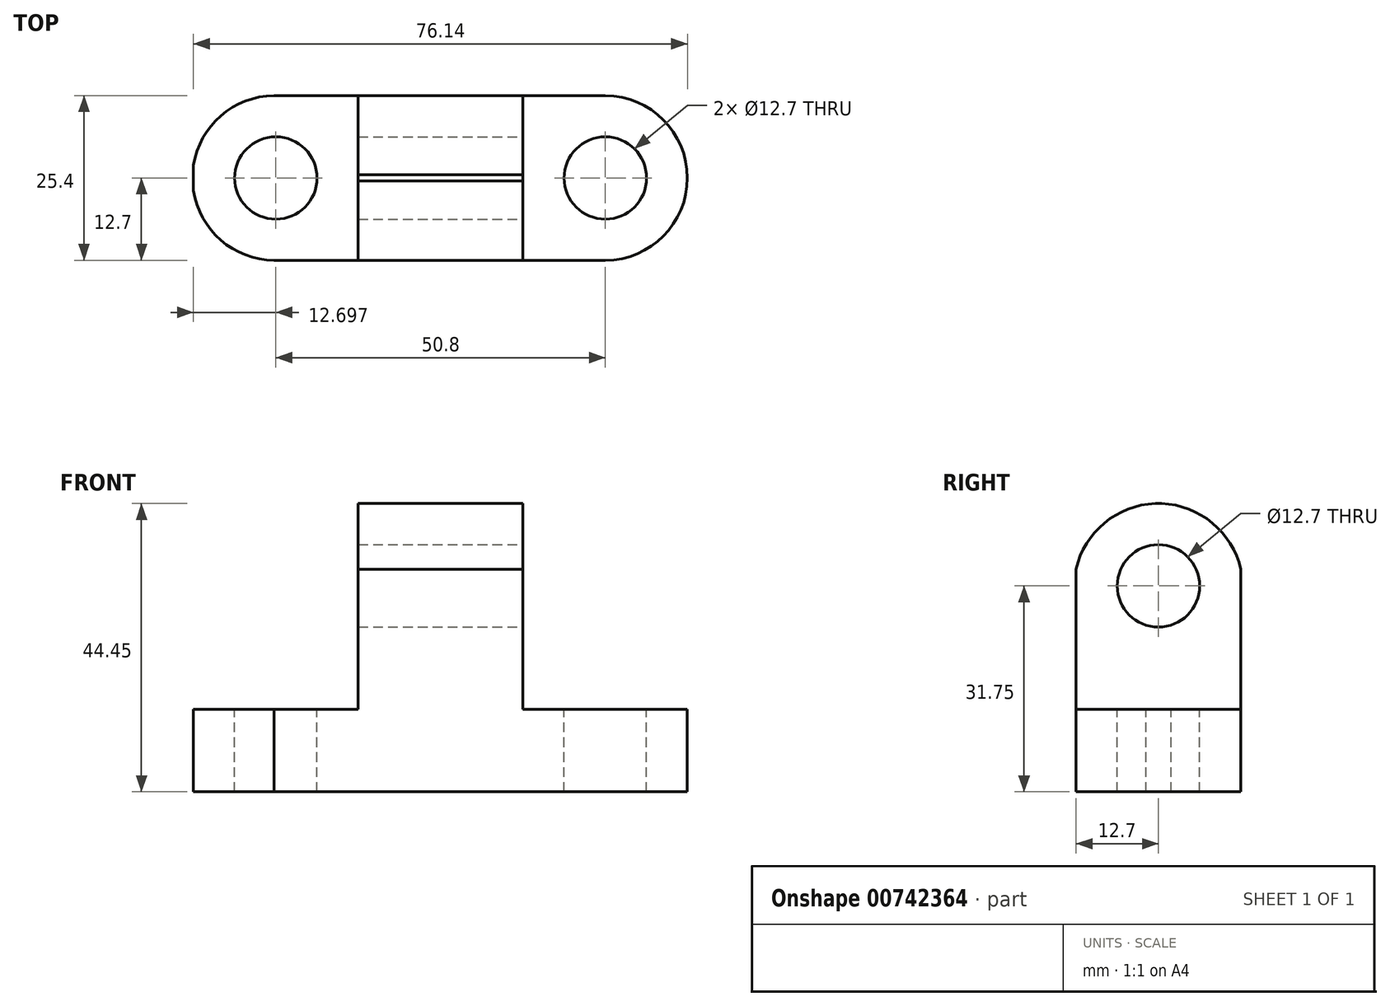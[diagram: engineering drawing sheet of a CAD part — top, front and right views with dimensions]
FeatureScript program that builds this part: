
annotation { "Feature Type Name" : "Feature", "Feature Type Description" : "" }
export const myFeature = defineFeature(function(context is Context, id is Id, definition is map)
    precondition{}
    {
        {
            var Q0;
            Q0=qCreatedBy(makeId("Front.planeOp"),FACE);
            var sketch = newSketch(context, id + "F0", { "sketchPlane" : qUnion([Q0])});
            skLineSegment(sketch, "E0", {"start": v(-40.6, 0) * mm, "end": v(35.6, 0) * mm});
            skLineSegment(sketch, "E1", {"start": v(35.6, 0) * mm, "end": v(35.6, 12.7) * mm});
            skLineSegment(sketch, "E2", {"start": v(35.6, 12.7) * mm, "end": v(10.2, 12.7) * mm});
            skLineSegment(sketch, "E3", {"start": v(10.2, 12.7) * mm, "end": v(10.2, 44.45) * mm});
            skLineSegment(sketch, "E4", {"start": v(10.2, 44.45) * mm, "end": v(-15.2, 44.45) * mm});
            skLineSegment(sketch, "E5", {"start": v(-15.2, 44.45) * mm, "end": v(-15.2, 12.7) * mm});
            skLineSegment(sketch, "E6", {"start": v(-15.2, 12.7) * mm, "end": v(-40.6, 12.7) * mm});
            skLineSegment(sketch, "E7", {"start": v(-40.6, 12.7) * mm, "end": v(-40.6, 0) * mm});
            skSolve(sketch);
        }
        {
            var Q0;
            Q0=makeQuery(id+"F0.imprint","IMPRINT",FACE,{"disambiguationData":[TD([[makeQuery(id+"F0.imprint","IMPRINT",EDGE,{"derivedFrom":sQuery(id+"F0.wireOp",EDGE,"E0")}),1.0]])]});
            extrude(context, id + "F1", {"entities" : qUnion([Q0]), "depth" : 25.4 * mm, "offsetDistance" : 25.4 * mm});
        }
        {
            var Q0;
            Q0=makeQuery(id+"F1.opExtrude","SWEPT_FACE",FACE,{"disambiguationData":[OSD([sQuery(id+"F0.wireOp",EDGE,"E6")])]});
            var sketch = newSketch(context, id + "F2", { "sketchPlane" : qUnion([Q0])});
            skCircle(sketch, "E8", {"center": v(-27.9, -12.7) * mm, "radius": 6.35 * mm});
            skArc(sketch, "E9", {"start": v(-27.9, 0) * mm, "mid": v(-40.75, -12.7) * mm, "end": v(-27.9, -25.4) * mm});
            skSolve(sketch);
        }
        {
            var Q0;
            Q0=makeQuery(id+"F2.imprint","IMPRINT",FACE,{"disambiguationData":[TD([[makeQuery(id+"F2.imprint","IMPRINT",EDGE,{"derivedFrom":sQuery(id+"F2.wireOp",EDGE,"E8")}),1.0]])]});
            var Q1;
            {var subQ0=sQuery(id+"F2.wireOp",EDGE,"E9");var subQ1=sQuery(id+"F0.wireOp",EDGE,"E6");var subQ4=makeQuery(id+"F1.opExtrude","CAP_EDGE",EDGE,{"disambiguationData":[OSD([subQ1])],"isStart":false});var subQ5=makeQuery(id+"F2.imprint","INTERSECT",VERTEX,{"disambiguationData":[OD(1.0)],"derivedFrom":[subQ4,subQ0]});Q1=makeQuery(id+"F2.imprint","IMPRINT",FACE,{"disambiguationData":[TD([[makeQuery(id+"F2.imprint","IMPRINT",EDGE,{"disambiguationData":[TD([[subQ5,1.0]])],"derivedFrom":subQ0}),-1.0]])]});}
            var Q2;
            {var subQ0=sQuery(id+"F2.wireOp",EDGE,"E9");var subQ1=sQuery(id+"F0.wireOp",EDGE,"E6");var subQ2=makeQuery(id+"F1.opExtrude","CAP_EDGE",EDGE,{"disambiguationData":[OSD([subQ1])],"isStart":true});var subQ3=makeQuery(id+"F2.imprint","INTERSECT",VERTEX,{"disambiguationData":[OD(1.0)],"derivedFrom":[subQ2,subQ0]});Q2=makeQuery(id+"F2.imprint","IMPRINT",FACE,{"disambiguationData":[TD([[makeQuery(id+"F2.imprint","IMPRINT",EDGE,{"disambiguationData":[TD([[subQ3,-1.0]])],"derivedFrom":subQ0}),-1.0]])]});}
            extrude(context, id + "F3", {"entities" : qUnion([Q0, Q1, Q2]), "operationType" : NewBodyOperationType.REMOVE, "endBound" : BoundingType.THROUGH_ALL, "oppositeDirection" : true, "depth" : 25.4 * mm, "offsetDistance" : 25.4 * mm});
        }
        {
            var Q0;
            Q0=makeQuery(id+"F1.opExtrude","SWEPT_FACE",FACE,{"disambiguationData":[OSD([sQuery(id+"F0.wireOp",EDGE,"E2")])]});
            var sketch = newSketch(context, id + "F4", { "sketchPlane" : qUnion([Q0])});
            skCircle(sketch, "E10", {"center": v(22.9, -12.7) * mm, "radius": 6.35 * mm});
            skArc(sketch, "E11", {"start": v(22.9, -25.4) * mm, "mid": v(35.54, -12.7) * mm, "end": v(22.9, 0) * mm});
            skSolve(sketch);
        }
        {
            var Q0;
            Q0=makeQuery(id+"F4.imprint","IMPRINT",FACE,{"disambiguationData":[TD([[makeQuery(id+"F4.imprint","IMPRINT",EDGE,{"derivedFrom":sQuery(id+"F4.wireOp",EDGE,"E10")}),1.0]])]});
            var Q1;
            {var subQ0=sQuery(id+"F4.wireOp",EDGE,"E11");Q1=makeQuery(id+"F4.imprint","IMPRINT",FACE,{"disambiguationData":[TD([[makeQuery(id+"F4.imprint","IMPRINT",EDGE,{"derivedFrom":subQ0}),-1.0]])]});}
            extrude(context, id + "F5", {"entities" : qUnion([Q0, Q1]), "operationType" : NewBodyOperationType.REMOVE, "endBound" : BoundingType.THROUGH_ALL, "oppositeDirection" : true, "depth" : 25.4 * mm, "offsetDistance" : 25.4 * mm});
        }
        {
            var Q0;
            Q0=makeQuery(id+"F1.opExtrude","SWEPT_FACE",FACE,{"disambiguationData":[OSD([sQuery(id+"F0.wireOp",EDGE,"E3")])]});
            var sketch = newSketch(context, id + "F6", { "sketchPlane" : qUnion([Q0])});
            skCircle(sketch, "E12", {"center": v(-12.7, 31.75) * mm, "radius": 6.35 * mm});
            skArc(sketch, "E13", {"start": v(0, 28.57) * mm, "mid": v(-12.7, 44.46) * mm, "end": v(-25.4, 28.58) * mm});
            skSolve(sketch);
        }
        {
            var Q0;
            {var subQ0=sQuery(id+"F6.wireOp",EDGE,"E13");var subQ1=sQuery(id+"F0.wireOp",EDGE,"E3");var subQ4=makeQuery(id+"F1.opExtrude","CAP_EDGE",EDGE,{"disambiguationData":[OSD([subQ1])],"isStart":false});var subQ5=makeQuery(id+"F6.imprint","INTERSECT",VERTEX,{"disambiguationData":[OD(1.0)],"derivedFrom":[subQ4,subQ0]});Q0=makeQuery(id+"F6.imprint","IMPRINT",FACE,{"disambiguationData":[TD([[makeQuery(id+"F6.imprint","IMPRINT",EDGE,{"disambiguationData":[TD([[subQ5,1.0]])],"derivedFrom":subQ0}),-1.0]])]});}
            var Q1;
            {var subQ0=sQuery(id+"F6.wireOp",EDGE,"E13");var subQ1=sQuery(id+"F0.wireOp",EDGE,"E3");var subQ2=makeQuery(id+"F1.opExtrude","CAP_EDGE",EDGE,{"disambiguationData":[OSD([subQ1])],"isStart":true});var subQ3=makeQuery(id+"F6.imprint","INTERSECT",VERTEX,{"disambiguationData":[OD(1.0)],"derivedFrom":[subQ2,subQ0]});Q1=makeQuery(id+"F6.imprint","IMPRINT",FACE,{"disambiguationData":[TD([[makeQuery(id+"F6.imprint","IMPRINT",EDGE,{"disambiguationData":[TD([[subQ3,-1.0]])],"derivedFrom":subQ0}),-1.0]])]});}
            var Q2;
            Q2=makeQuery(id+"F6.imprint","IMPRINT",FACE,{"disambiguationData":[TD([[makeQuery(id+"F6.imprint","IMPRINT",EDGE,{"derivedFrom":sQuery(id+"F6.wireOp",EDGE,"E12")}),1.0]])]});
            extrude(context, id + "F7", {"entities" : qUnion([Q0, Q1, Q2]), "operationType" : NewBodyOperationType.REMOVE, "endBound" : BoundingType.THROUGH_ALL, "oppositeDirection" : true, "depth" : 25.4 * mm, "offsetDistance" : 25.4 * mm});
        }
    });
